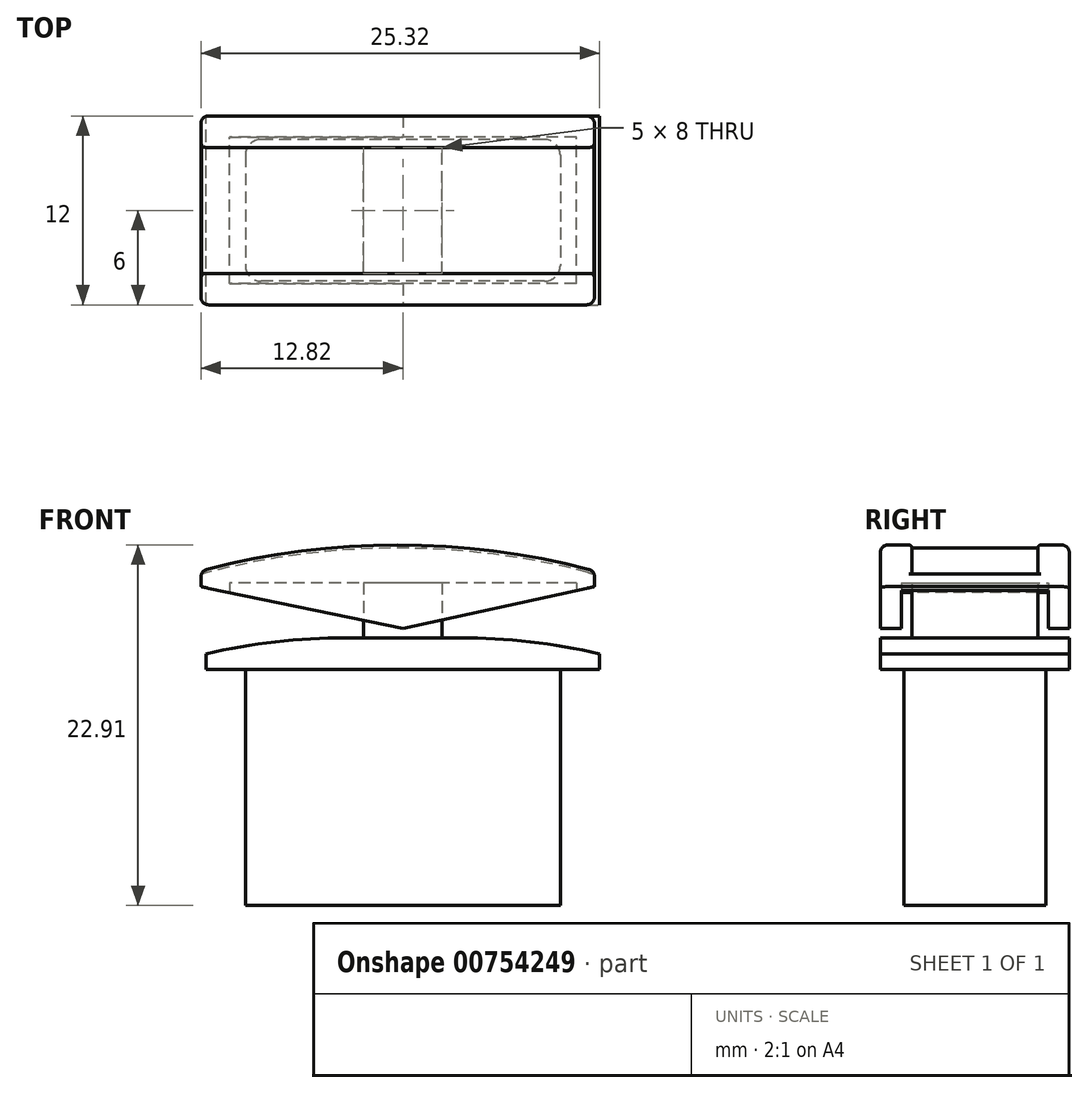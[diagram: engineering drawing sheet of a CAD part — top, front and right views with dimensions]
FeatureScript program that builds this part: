
annotation { "Feature Type Name" : "Feature", "Feature Type Description" : "" }
export const myFeature = defineFeature(function(context is Context, id is Id, definition is map)
    precondition{}
    {
        {
            var Q0;
            Q0=qCreatedBy(makeId("Top.planeOp"),FACE);
            var sketch = newSketch(context, id + "F0", { "sketchPlane" : qUnion([Q0])});
            skLineSegment(sketch, "E0.bottom", {"start": v(12.5, -6) * mm, "end": v(-12.5, -6) * mm});
            skLineSegment(sketch, "E0.top", {"start": v(12.5, 6) * mm, "end": v(-12.5, 6) * mm});
            skLineSegment(sketch, "E0.left", {"start": v(12.5, -6) * mm, "end": v(12.5, 6) * mm});
            skLineSegment(sketch, "E0.right", {"start": v(-12.5, -6) * mm, "end": v(-12.5, 6) * mm});
            skPoint(sketch, "E0.middle", {"position": v(0, 0) * mm});
            skSolve(sketch);
        }
        {
            var Q0;
            Q0=makeQuery(id+"F0.imprint","IMPRINT",FACE,{"disambiguationData":[TD([[makeQuery(id+"F0.imprint","IMPRINT",EDGE,{"derivedFrom":sQuery(id+"F0.wireOp",EDGE,"E0.bottom")}),-1.0]])]});
            extrude(context, id + "F1", {"entities" : qUnion([Q0]), "depth" : 1 * mm, "offsetDistance" : 25 * mm});
        }
        {
            var Q0;
            Q0=makeQuery(id+"F1.opExtrude","CAP_EDGE",EDGE,{"disambiguationData":[OSD([sQuery(id+"F0.wireOp",EDGE,"E0.left")])],"isStart":false});
            var Q1;
            Q1=makeQuery(id+"F1.opExtrude","CAP_EDGE",EDGE,{"disambiguationData":[OSD([sQuery(id+"F0.wireOp",EDGE,"E0.right")])],"isStart":false});
            fillet(context, id + "F2", {"entities" : qUnion([Q0, Q1]), "radius" : 40 * mm, "tangentPropagation" : true, "rho" : 0.5, "crossSection" : FilletCrossSection.CONIC, "allowEdgeOverflow" : false});
        }
        {
            var Q0;
            Q0=makeQuery(id+"F1.opExtrude","CAP_FACE",FACE,{"disambiguationData":[OSD([sQuery(id+"F0.wireOp",EDGE,"E0.bottom"),sQuery(id+"F0.wireOp",EDGE,"E0.top"),sQuery(id+"F0.wireOp",EDGE,"E0.left"),sQuery(id+"F0.wireOp",EDGE,"E0.right")])],"isStart":true});
            var Q1;
            Q1 = qSketchRegion(id + "F0", true);
            extrude(context, id + "F3", {"entities" : qUnion([Q0, Q1]), "operationType" : NewBodyOperationType.ADD, "depth" : 1 * mm, "offsetDistance" : 25 * mm});
        }
        {
            var Q0;
            {var subQ0=sQuery(id+"F0.wireOp",EDGE,"E0.right");var subQ1=sQuery(id+"F0.wireOp",EDGE,"E0.left");var subQ2=sQuery(id+"F0.wireOp",EDGE,"E0.top");var subQ3=sQuery(id+"F0.wireOp",EDGE,"E0.bottom");Q0=makeQuery(id+"F3.opExtrude","CAP_FACE",FACE,{"disambiguationData":[OSD([subQ3,subQ2,subQ1,subQ0]),TDD([makeQuery(id+"F0.imprint","IMPRINT",EDGE,{"derivedFrom":subQ3}),makeQuery(id+"F0.imprint","IMPRINT",EDGE,{"derivedFrom":subQ2}),makeQuery(id+"F0.imprint","IMPRINT",EDGE,{"derivedFrom":subQ1}),makeQuery(id+"F0.imprint","IMPRINT",EDGE,{"derivedFrom":subQ0})])],"isStart":false});}
            var sketch = newSketch(context, id + "F4", { "sketchPlane" : qUnion([Q0])});
            skLineSegment(sketch, "E1.bottom", {"start": v(10, -4.5) * mm, "end": v(-10, -4.5) * mm});
            skLineSegment(sketch, "E1.top", {"start": v(10, 4.5) * mm, "end": v(-10, 4.5) * mm});
            skLineSegment(sketch, "E1.left", {"start": v(10, -4.5) * mm, "end": v(10, 4.5) * mm});
            skLineSegment(sketch, "E1.right", {"start": v(-10, -4.5) * mm, "end": v(-10, 4.5) * mm});
            skPoint(sketch, "E1.middle", {"position": v(0, 0) * mm});
            skSolve(sketch);
        }
        {
            var Q0;
            Q0=makeQuery(id+"F4.imprint","IMPRINT",FACE,{"disambiguationData":[TD([[makeQuery(id+"F4.imprint","IMPRINT",EDGE,{"derivedFrom":sQuery(id+"F4.wireOp",EDGE,"E1.bottom")}),-1.0]])]});
            extrude(context, id + "F5", {"entities" : qUnion([Q0]), "operationType" : NewBodyOperationType.ADD, "depth" : 15 * mm, "offsetDistance" : 25 * mm});
        }
        {
            var Q0;
            Q0=makeQuery(id+"F1.opExtrude","CAP_FACE",FACE,{"disambiguationData":[OSD([sQuery(id+"F0.wireOp",EDGE,"E0.bottom"),sQuery(id+"F0.wireOp",EDGE,"E0.top"),sQuery(id+"F0.wireOp",EDGE,"E0.left"),sQuery(id+"F0.wireOp",EDGE,"E0.right")])],"isStart":false});
            var sketch = newSketch(context, id + "F6", { "sketchPlane" : qUnion([Q0])});
            skLineSegment(sketch, "E2.bottom", {"start": v(2.5, -4) * mm, "end": v(-2.5, -4) * mm});
            skLineSegment(sketch, "E2.top", {"start": v(2.5, 4) * mm, "end": v(-2.5, 4) * mm});
            skLineSegment(sketch, "E2.left", {"start": v(2.5, -4) * mm, "end": v(2.5, 4) * mm});
            skLineSegment(sketch, "E2.right", {"start": v(-2.5, -4) * mm, "end": v(-2.5, 4) * mm});
            skPoint(sketch, "E2.middle", {"position": v(0, 0) * mm});
            skSolve(sketch);
        }
        {
            var Q0;
            Q0=makeQuery(id+"F6.imprint","IMPRINT",FACE,{"disambiguationData":[TD([[makeQuery(id+"F6.imprint","IMPRINT",EDGE,{"derivedFrom":sQuery(id+"F6.wireOp",EDGE,"E2.bottom")}),-1.0]])]});
            extrude(context, id + "F7", {"entities" : qUnion([Q0]), "operationType" : NewBodyOperationType.ADD, "depth" : 4 * mm, "offsetDistance" : 25 * mm});
        }
        {
            var Q0;
            Q0=makeQuery(id+"F7.opExtrude","SWEPT_FACE",FACE,{"disambiguationData":[OSD([sQuery(id+"F6.wireOp",EDGE,"E2.bottom")])]});
            var sketch = newSketch(context, id + "F8", { "sketchPlane" : qUnion([Q0])});
            skPoint(sketch, "E3", {"position": v(0, 3) * mm});
            skPoint(sketch, "E3.positionSnap0", {"position": v(0, 5) * mm});
            skSolve(sketch);
        }
        {
            var Q0;
            {var subQ0=sQuery(id+"F6.wireOp",EDGE,"E2.bottom");Q0=makeQuery(id+"F8.imprint","IMPRINT",FACE,{"disambiguationData":[TD([[makeQuery(id+"F8.imprint","IMPRINT",EDGE,{"derivedFrom":makeQuery(id+"F7.opExtrude","CAP_EDGE",EDGE,{"disambiguationData":[OSD([subQ0])],"isStart":false})}),1.0]])]});}
            var sketch = newSketch(context, id + "F9", { "sketchPlane" : qUnion([Q0])});
            skLineSegment(sketch, "E4", {"start": v(0, 1.6) * mm, "end": v(12.18, 4.26) * mm});
            skLineSegment(sketch, "E5", {"start": v(12.18, 4.26) * mm, "end": v(12.18, 5.26) * mm});
            skLineSegment(sketch, "E6", {"start": v(0, 1.6) * mm, "end": v(-12.82, 4.26) * mm});
            skLineSegment(sketch, "E7", {"start": v(-12.82, 4.26) * mm, "end": v(-12.82, 5.26) * mm});
            skLineSegment(sketch, "E8", {"start": v(-12.82, 5.26) * mm, "end": v(12.18, 5.26) * mm});
            skArc(sketch, "E9", {"start": v(12.18, 5.26) * mm, "mid": v(-0.32, 6.91) * mm, "end": v(-12.82, 5.26) * mm});
            skSolve(sketch);
        }
        {
            var Q0;
            Q0 = qSketchRegion(id + "F9", true);
            extrude(context, id + "F10", {"entities" : qUnion([Q0]), "operationType" : NewBodyOperationType.ADD, "oppositeDirection" : true, "depth" : 10 * mm, "offsetDistance" : 25 * mm, "hasSecondDirection" : true, "secondDirectionOppositeDirection" : false, "secondDirectionDepth" : 2 * mm});
        }
        {
            var Q0;
            Q0=makeQuery(id+"F10.opExtrude","SWEPT_FACE",FACE,{"disambiguationData":[OSD([sQuery(id+"F9.wireOp",EDGE,"E9")])]});
            var Q1;
            Q1=makeQuery(id+"F10.opExtrude","CAP_EDGE",EDGE,{"disambiguationData":[OSD([sQuery(id+"F9.wireOp",EDGE,"E5")])],"isStart":true});
            var Q2;
            Q2=makeQuery(id+"F10.opExtrude","CAP_EDGE",EDGE,{"disambiguationData":[OSD([sQuery(id+"F9.wireOp",EDGE,"E7")])],"isStart":true});
            var Q3;
            Q3=makeQuery(id+"F10.opExtrude","CAP_EDGE",EDGE,{"disambiguationData":[OSD([sQuery(id+"F9.wireOp",EDGE,"E7")])],"isStart":false});
            var Q4;
            Q4=makeQuery(id+"F10.opExtrude","CAP_EDGE",EDGE,{"disambiguationData":[OSD([sQuery(id+"F9.wireOp",EDGE,"E5")])],"isStart":false});
            fillet(context, id + "F11", {"entities" : qUnion([Q0, Q1, Q2, Q3, Q4]), "radius" : 0.5 * mm, "tangentPropagation" : true, "allowEdgeOverflow" : false});
        }
        {
            var Q0;
            Q0=makeQuery(id+"F1.opExtrude","CAP_FACE",FACE,{"disambiguationData":[OSD([sQuery(id+"F0.wireOp",EDGE,"E0.bottom"),sQuery(id+"F0.wireOp",EDGE,"E0.top"),sQuery(id+"F0.wireOp",EDGE,"E0.left"),sQuery(id+"F0.wireOp",EDGE,"E0.right")])],"isStart":false});
            var sketch = newSketch(context, id + "F12", { "sketchPlane" : qUnion([Q0])});
            skLineSegment(sketch, "E10.bottom", {"start": v(11.02, -4.66) * mm, "end": v(-11.02, -4.66) * mm});
            skLineSegment(sketch, "E10.top", {"start": v(11.02, 4.66) * mm, "end": v(-11.02, 4.66) * mm});
            skLineSegment(sketch, "E10.left", {"start": v(11.02, -4.66) * mm, "end": v(11.02, 4.66) * mm});
            skLineSegment(sketch, "E10.right", {"start": v(-11.02, -4.66) * mm, "end": v(-11.02, 4.66) * mm});
            skPoint(sketch, "E10.middle", {"position": v(0, 0) * mm});
            skLineSegment(sketch, "E11.bottom", {"start": v(2.5, -4) * mm, "end": v(-2.5, -4) * mm});
            skLineSegment(sketch, "E11.top", {"start": v(2.5, 4) * mm, "end": v(-2.5, 4) * mm});
            skLineSegment(sketch, "E11.left", {"start": v(2.5, -4) * mm, "end": v(2.5, 4) * mm});
            skLineSegment(sketch, "E11.right", {"start": v(-2.5, -4) * mm, "end": v(-2.5, 4) * mm});
            skSolve(sketch);
        }
        {
            var Q0;
            Q0 = qSketchRegion(id + "F12", true);
            var Q1;
            {var subQ0=sQuery(id+"F12.wireOp",EDGE,"E10.right");Q1=makeQuery(id+"F12.imprint","IMPRINT",FACE,{"disambiguationData":[TD([[makeQuery(id+"F12.imprint","IMPRINT",EDGE,{"derivedFrom":subQ0}),-1.0]])]});}
            extrude(context, id + "F13", {"entities" : qUnion([Q0, Q1]), "operationType" : NewBodyOperationType.REMOVE, "depth" : 3.5 * mm, "offsetDistance" : 25 * mm});
        }
        {
            var Q0;
            {var subQ0=sQuery(id+"F6.wireOp",EDGE,"E2.bottom");Q0=makeQuery(id+"F8.imprint","IMPRINT",FACE,{"disambiguationData":[TD([[makeQuery(id+"F8.imprint","IMPRINT",EDGE,{"derivedFrom":makeQuery(id+"F7.opExtrude","CAP_EDGE",EDGE,{"disambiguationData":[OSD([subQ0])],"isStart":false})}),1.0]])]});}
            var sketch = newSketch(context, id + "F14", { "sketchPlane" : qUnion([Q0])});
            skCircle(sketch, "E12", {"center": v(0, 3.01) * mm, "radius": 0.66 * mm});
            skSolve(sketch);
        }
        {
            var Q0;
            Q0=sQuery(id+"F14.wireOp",EDGE,"E12");
            extrude(context, id + "F15", {"bodyType" : ToolBodyType.SURFACE, "surfaceEntities" : qUnion([Q0]), "depth" : 1 * mm, "offsetDistance" : 25 * mm, "hasSecondDirection" : true, "secondDirectionOppositeDirection" : true, "secondDirectionDepth" : 9 * mm});
        }
        {
            var Q0;
            Q0=makeQuery(id+"F5.opExtrude","SWEPT_EDGE",EDGE,{"disambiguationData":[OSD([sQuery(id+"F4.wireOp",EDGE,"E1.top"),sQuery(id+"F4.wireOp",EDGE,"E1.right")])]});
            var Q1;
            Q1=makeQuery(id+"F5.opExtrude","SWEPT_EDGE",EDGE,{"disambiguationData":[OSD([sQuery(id+"F4.wireOp",EDGE,"E1.top"),sQuery(id+"F4.wireOp",EDGE,"E1.left")])]});
            var Q2;
            Q2=makeQuery(id+"F5.opExtrude","SWEPT_EDGE",EDGE,{"disambiguationData":[OSD([sQuery(id+"F4.wireOp",EDGE,"E1.bottom"),sQuery(id+"F4.wireOp",EDGE,"E1.right")])]});
            var Q3;
            Q3=makeQuery(id+"F5.opExtrude","SWEPT_EDGE",EDGE,{"disambiguationData":[OSD([sQuery(id+"F4.wireOp",EDGE,"E1.bottom"),sQuery(id+"F4.wireOp",EDGE,"E1.left")])]});
            fillet(context, id + "F16", {"entities" : qUnion([Q0, Q1, Q2, Q3]), "radius" : 1 * mm, "tangentPropagation" : true, "allowEdgeOverflow" : false});
        }
        {
            var Q0;
            Q0=qCreatedBy(makeId("Front.planeOp"),FACE);
            var sketch = newSketch(context, id + "F17", { "sketchPlane" : qUnion([Q0])});
            skArc(sketch, "E13.0", {"start": v(-13, 5) * mm, "mid": v(0.01, 6.71) * mm, "end": v(13, 4.82) * mm});
            skLineSegment(sketch, "E14", {"start": v(-13, 5) * mm, "end": v(-13, 7.2) * mm});
            skLineSegment(sketch, "E15", {"start": v(-13, 7.2) * mm, "end": v(13, 7.2) * mm});
            skLineSegment(sketch, "E16", {"start": v(13, 7.2) * mm, "end": v(13, 4.82) * mm});
            skSolve(sketch);
        }
        {
            var Q0;
            Q0 = qSketchRegion(id + "F17", true);
            extrude(context, id + "F18", {"entities" : qUnion([Q0]), "operationType" : NewBodyOperationType.REMOVE, "endBound" : BoundingType.SYMMETRIC, "oppositeDirection" : true, "depth" : 8 * mm, "offsetDistance" : 25 * mm});
        }
        {
            var Q0;
            Q0=makeQuery(id+"F18.boolean.opBoolean","INTERSECT",EDGE,{"derivedFrom":[makeQuery(id+"F10.opExtrude","SWEPT_FACE",FACE,{"disambiguationData":[OSD([sQuery(id+"F9.wireOp",EDGE,"E9")])]}),makeQuery(id+"F18.opExtrude","CAP_FACE",FACE,{"disambiguationData":[OSD([sQuery(id+"F17.wireOp",EDGE,"E13.0"),sQuery(id+"F17.wireOp",EDGE,"E14"),sQuery(id+"F17.wireOp",EDGE,"E15"),sQuery(id+"F17.wireOp",EDGE,"E16")])],"isStart":true})]});
            var Q1;
            Q1=makeQuery(id+"F18.boolean.opBoolean","INTERSECT",EDGE,{"derivedFrom":[makeQuery(id+"F10.opExtrude","SWEPT_FACE",FACE,{"disambiguationData":[OSD([sQuery(id+"F9.wireOp",EDGE,"E9")])]}),makeQuery(id+"F18.opExtrude","CAP_FACE",FACE,{"disambiguationData":[OSD([sQuery(id+"F17.wireOp",EDGE,"E13.0"),sQuery(id+"F17.wireOp",EDGE,"E14"),sQuery(id+"F17.wireOp",EDGE,"E15"),sQuery(id+"F17.wireOp",EDGE,"E16")])],"isStart":false})]});
            fillet(context, id + "F19", {"entities" : qUnion([Q0, Q1]), "radius" : 0.2 * mm, "tangentPropagation" : true, "allowEdgeOverflow" : false});
        }
    });
